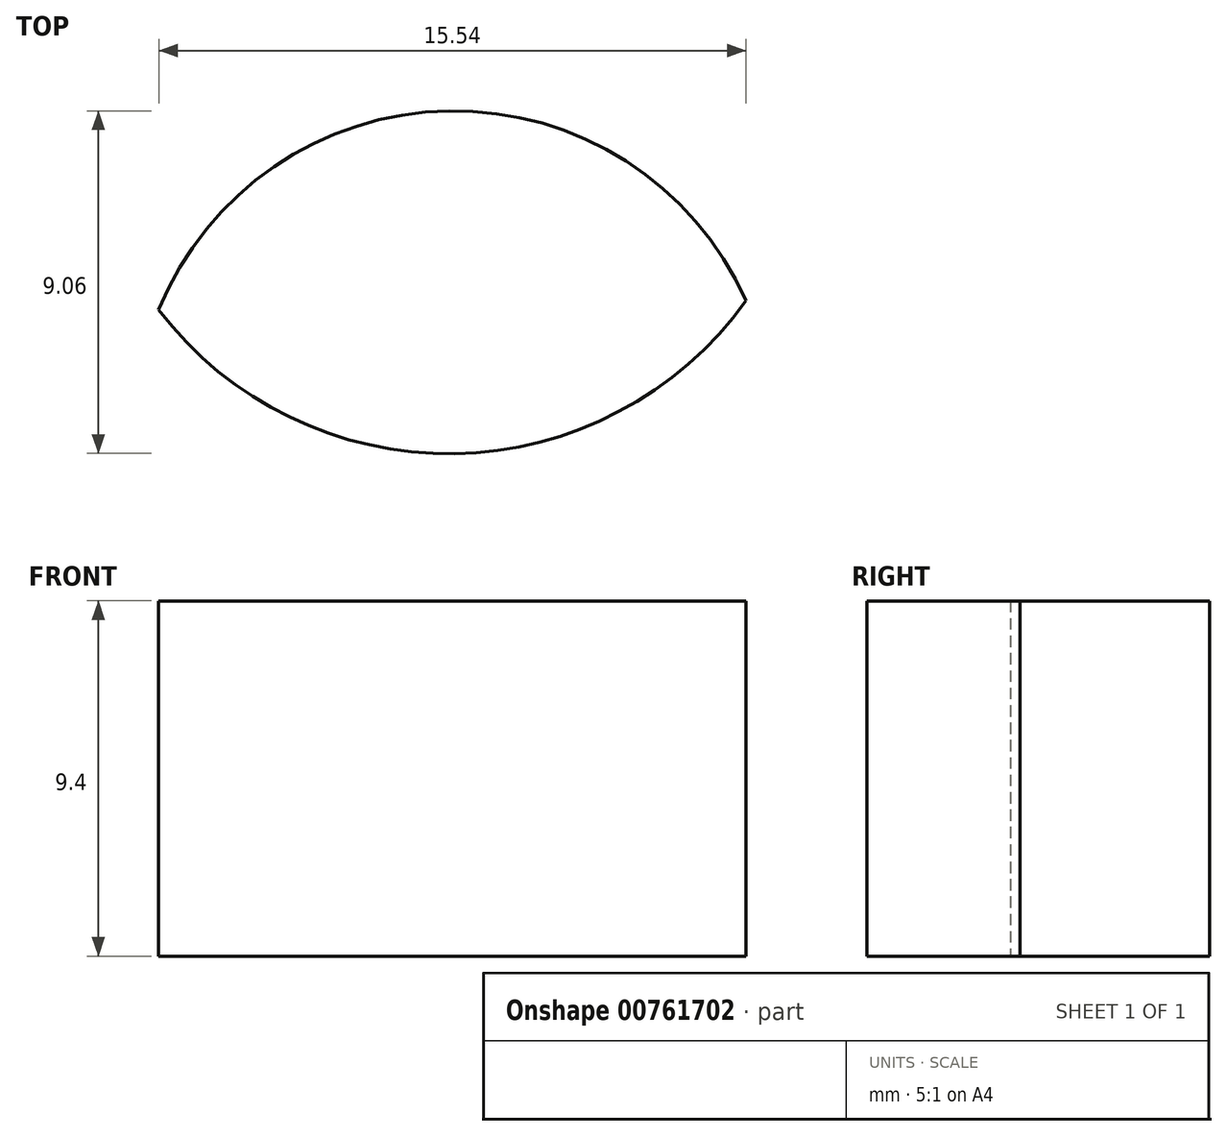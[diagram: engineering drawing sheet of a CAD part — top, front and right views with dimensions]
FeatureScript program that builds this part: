
annotation { "Feature Type Name" : "Feature", "Feature Type Description" : "" }
export const myFeature = defineFeature(function(context is Context, id is Id, definition is map)
    precondition{}
    {
        {
            var Q0;
            Q0=qCreatedBy(makeId("Top.planeOp"),FACE);
            var sketch = newSketch(context, id + "F0", { "sketchPlane" : qUnion([Q0])});
            skArc(sketch, "E0", {"start": v(7.79, 23.21) * mm, "mid": v(-0.06, 28.23) * mm, "end": v(-7.75, 22.97) * mm});
            skArc(sketch, "E1", {"start": v(-7.75, 22.97) * mm, "mid": v(0.08, 19.17) * mm, "end": v(7.79, 23.21) * mm});
            skSolve(sketch);
        }
        {
            var Q0;
            Q0 = qSketchRegion(id + "F0", true);
            extrude(context, id + "F1", {"entities" : qUnion([Q0]), "depth" : 9.4 * mm, "offsetDistance" : 25.4 * mm});
        }
    });
